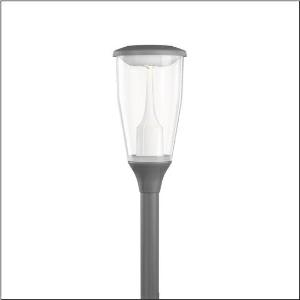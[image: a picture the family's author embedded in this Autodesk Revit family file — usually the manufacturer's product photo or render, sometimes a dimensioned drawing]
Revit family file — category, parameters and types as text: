
# Revit family: dl_11_iq___st1_2a_5xa5565af14h000022_cb01
name_source: partatom
category: Lighting Fixtures
units: mm (PartAtom-declared; Revit-internal decimal feet)

## family parameters
Cut with Voids When Loaded = No
Host = Face
Light Source = No
Part Type = Normal
Room Calculation Point = No
Round Connector Dimension = Use Diameter
Shared = No

## types (1)
- --- (1 x LED, 1560 lm, 12.9 W, 2200K)
    Apparent Load = 13 VA
    CIE Flux Codes = 24 63 94 96 100
    Color Rendering = 70
    Color Temperature = 2200K
    Default Elevation = 1800 mm
    Description = DL 11 iQ, mast luminaire, Module 540 iQ-SR, primary light control with 3 zone facetted reflector, of plastic, silver coated, highly specular, structured, primary optical cover: cover, of PMMA, transparent, light distribution: ST1.2a, light emission: direct distribution, primary light characteristic: asymmetric, installation type: post-top, LED, High Power LED, rated luminous flux: 1.560lm, luminous efficacy: 149lm/W, light colour: 722, colour temperature: 2200K, control: Street-Remote, Auto-Match, Temp-Guard, Lumen-Switch, Night-Set, Smart-Wire, Light-Fading, Desk-Remote (wireless, voltage-free reading and setting of iQ features in the workshop via application-optimized NFC function/RFID function), optimised constant luminous flux control (CLO 2.0), mains connection: 220..240V, AC, 50/60Hz, connection cable pre-assembled, cable length: 5,5m, start of lifetime: 13W, end of service life: 13W, reduction: 5W, luminaire housing, upper part, of diecast aluminium, coated, Siteco® metallic grey (DB 702S), spigot size: 60mm (post-top), post-top mast mounting element, of diecast aluminium, coated, Siteco® metallic grey (DB 702S), Module 540 iQ-SR, traffic white (RAL 9016), equipment: standard, protection rating (complete): IP66, insulation class (complete): insulation class II (safety insulation), certification: CE, ENEC, ENEC+, VDE, packaging unit: 1 piece

Light Distribution: ST1.2a
    Height = 665 mm
    Lamp = 1 x LED
    Lamp Light Flux = 1560 lm
    Lamp Power = 12.9 W
    Lamp count = 1
    Length = 334 mm
    Luminous efficacy = 121 lm/W
    Manufacturer = Siteco
    ModVariant = No
    Model = 5XA5565AF14H000022
    Number of Poles = 1
    OnlyDefault = Yes
    Power Factor = 1
    Product Name = DL 11 iQ | ST1.2a
    Product group = mast luminaire | pylon top
    ProductGroupID = 6100
    Protection Class = Protection class II
    Protection Degree = IP 66
    RLX_Detail_Level = 1
    RLX_Emergency_Light_Flux = 0 lm
    RLX_Emergency_Type = 0
    RLX_Emergency_Type_DB = No
    RlxData = <blob elided: 152689 chars, md5=436b5824>
    Socket = socket
    Standby Power = 0 W
    System Light Flux = 1560 lm
    System Power = 13 W
    Type Comments = factory setting: luminous flux: 100 % | dim-lin: 254 | 516 mA
    Type Image = l_1258354.jpg
    URL = http://relux.com
    VarID = @adj_044093
    Voltage = 0 V
    Weight = 0.00 kg
    Width = 0 mm  [stored 0 ft]

note: [stored X ft] marks values corroborated as IEEE doubles in the binary element streams (Revit-internal decimal feet)

## geometry (parser evidence)
native form markers: Blend x4, Sweep x12
no freeform markers — native parametric forms only
